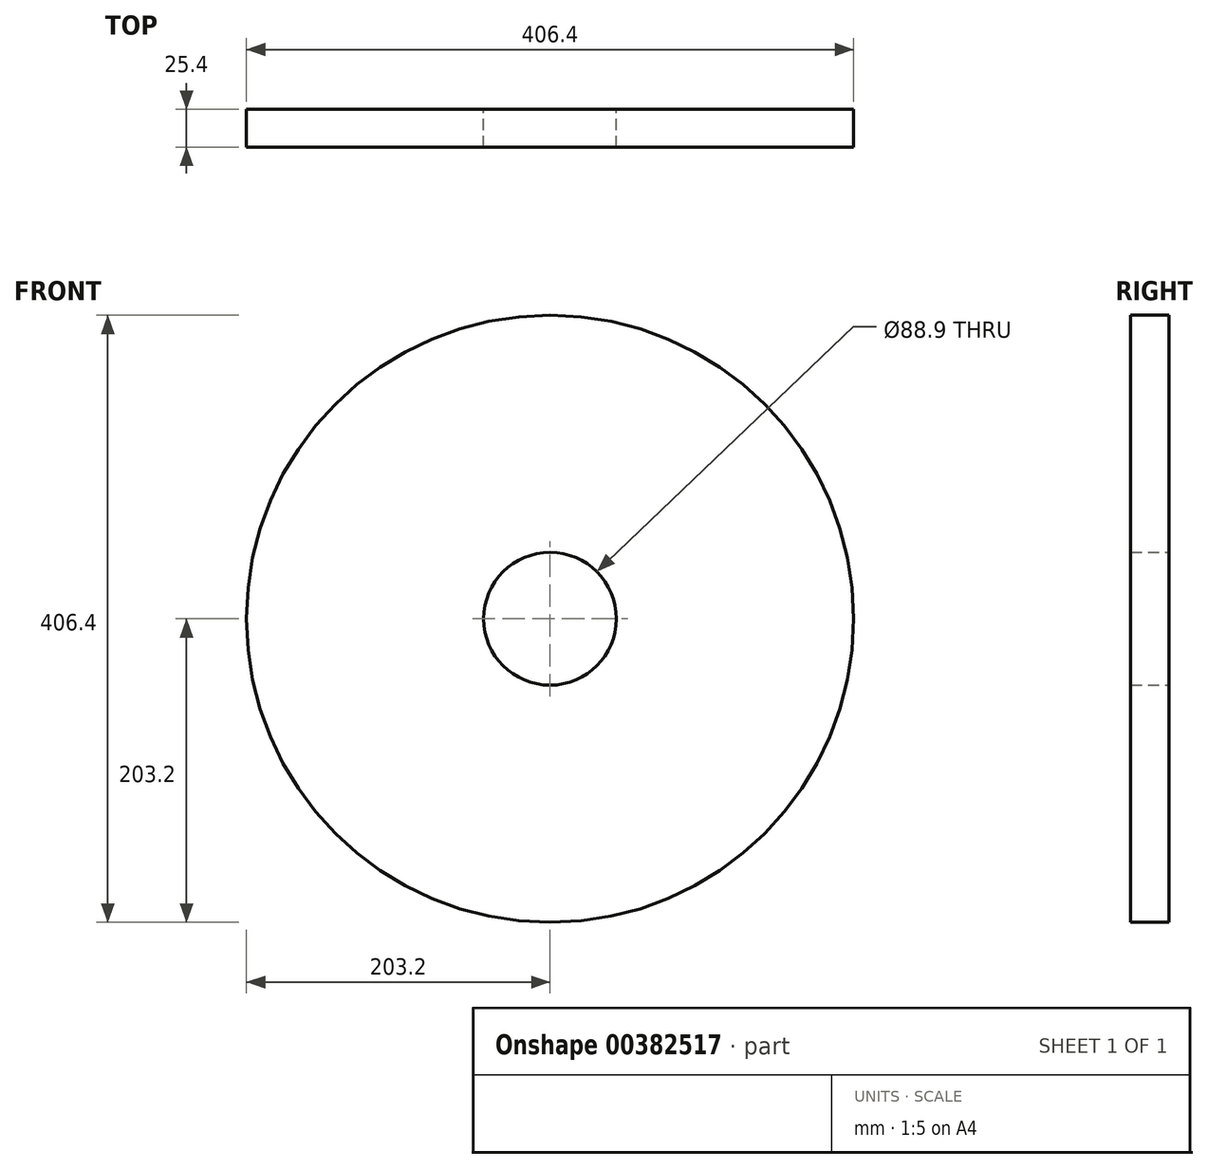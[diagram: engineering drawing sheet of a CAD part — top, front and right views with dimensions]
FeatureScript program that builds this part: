
annotation { "Feature Type Name" : "Feature", "Feature Type Description" : "" }
export const myFeature = defineFeature(function(context is Context, id is Id, definition is map)
    precondition{}
    {
        {
            var Q0;
            Q0=qCreatedBy(makeId("Front.planeOp"),FACE);
            var sketch = newSketch(context, id + "F0", { "sketchPlane" : qUnion([Q0])});
            skCircle(sketch, "E0.0", {"center": v(0, 0) * mm, "radius": 203.2 * mm});
            skCircle(sketch, "E1.0", {"center": v(0, 0) * mm, "radius": 44.45 * mm});
            skSolve(sketch);
        }
        {
            var Q0;
            Q0=qSketchRegion(id+"F0",true);
            extrude(context, id + "F1", {"entities" : qUnion([Q0]), "depth" : 25.4 * mm});
        }
    });
